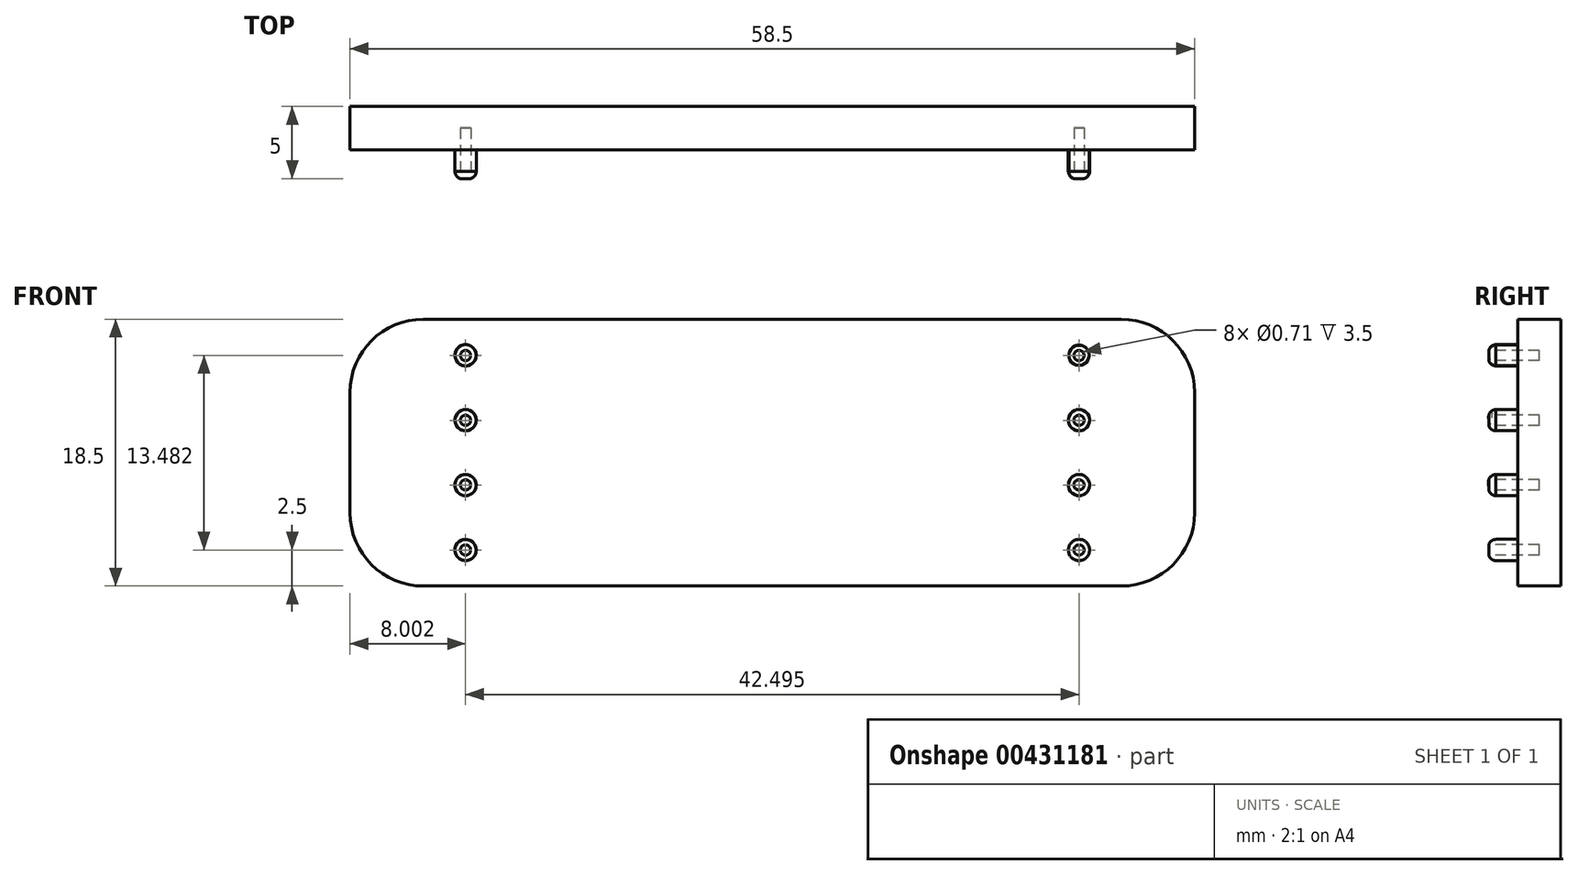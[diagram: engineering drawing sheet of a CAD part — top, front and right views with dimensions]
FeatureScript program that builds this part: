
annotation { "Feature Type Name" : "Feature", "Feature Type Description" : "" }
export const myFeature = defineFeature(function(context is Context, id is Id, definition is map)
    precondition{}
    {
        {
            var Q0;
            Q0=qCreatedBy(makeId("Front.planeOp"),FACE);
            var sketch = newSketch(context, id + "F0", { "sketchPlane" : qUnion([Q0])});
            skLineSegment(sketch, "E0.bottom", {"start": v(29.25, 9.25) * mm, "end": v(-29.25, 9.25) * mm});
            skLineSegment(sketch, "E0.top", {"start": v(29.25, -9.25) * mm, "end": v(-29.25, -9.25) * mm});
            skLineSegment(sketch, "E0.left", {"start": v(29.25, 9.25) * mm, "end": v(29.25, -9.25) * mm});
            skLineSegment(sketch, "E0.right", {"start": v(-29.25, 9.25) * mm, "end": v(-29.25, -9.25) * mm});
            skPoint(sketch, "E0.middle", {"position": v(0, 0) * mm});
            skSolve(sketch);
        }
        {
            var Q0;
            Q0=makeQuery(id+"F0.imprint","IMPRINT",FACE,{"disambiguationData":[TD([[makeQuery(id+"F0.imprint","IMPRINT",EDGE,{"derivedFrom":sQuery(id+"F0.wireOp",EDGE,"E0.bottom")}),1.0]])]});
            extrude(context, id + "F1", {"entities" : qUnion([Q0]), "depth" : 3 * mm});
        }
        {
            var Q0;
            Q0=makeQuery(id+"F1.opExtrude","CAP_FACE",FACE,{"disambiguationData":[OSD([sQuery(id+"F0.wireOp",EDGE,"E0.bottom"),sQuery(id+"F0.wireOp",EDGE,"E0.top"),sQuery(id+"F0.wireOp",EDGE,"E0.left"),sQuery(id+"F0.wireOp",EDGE,"E0.right")])],"isStart":false});
            var sketch = newSketch(context, id + "F2", { "sketchPlane" : qUnion([Q0])});
            skCircle(sketch, "E1", {"center": v(21.25, 6.75) * mm, "radius": 0.7 * mm});
            skCircle(sketch, "E2", {"center": v(21.25, 2.25) * mm, "radius": 0.74 * mm});
            skCircle(sketch, "E3", {"center": v(21.25, -2.25) * mm, "radius": 0.74 * mm});
            skCircle(sketch, "E4", {"center": v(21.25, -6.75) * mm, "radius": 0.74 * mm});
            skCircle(sketch, "E5", {"center": v(-21.25, 6.75) * mm, "radius": 0.74 * mm});
            skCircle(sketch, "E6", {"center": v(-21.25, 2.25) * mm, "radius": 0.74 * mm});
            skCircle(sketch, "E7", {"center": v(-21.25, -2.25) * mm, "radius": 0.74 * mm});
            skCircle(sketch, "E8", {"center": v(-21.25, -6.75) * mm, "radius": 0.74 * mm});
            skSolve(sketch);
        }
        {
            var Q0;
            Q0 = qSketchRegion(id + "F2", true);
            extrude(context, id + "F3", {"entities" : qUnion([Q0]), "operationType" : NewBodyOperationType.ADD, "depth" : 2 * mm});
        }
        {
            var Q0;
            Q0=makeQuery(id+"F3.opExtrude","CAP_FACE",FACE,{"disambiguationData":[OSD([sQuery(id+"F2.wireOp",EDGE,"E4")])],"isStart":false});
            var sketch = newSketch(context, id + "F4", { "sketchPlane" : qUnion([Q0])});
            skCircle(sketch, "E9", {"center": v(21.25, -6.75) * mm, "radius": 0.36 * mm});
            skCircle(sketch, "E10", {"center": v(21.25, -2.24) * mm, "radius": 0.36 * mm});
            skCircle(sketch, "E11", {"center": v(21.25, 2.24) * mm, "radius": 0.36 * mm});
            skCircle(sketch, "E12", {"center": v(21.25, 6.73) * mm, "radius": 0.36 * mm});
            skCircle(sketch, "E13", {"center": v(-21.25, -6.75) * mm, "radius": 0.36 * mm});
            skCircle(sketch, "E14", {"center": v(-21.25, -2.24) * mm, "radius": 0.36 * mm});
            skCircle(sketch, "E15", {"center": v(-21.25, 2.24) * mm, "radius": 0.36 * mm});
            skCircle(sketch, "E16", {"center": v(-21.25, 6.73) * mm, "radius": 0.36 * mm});
            skSolve(sketch);
        }
        {
            var Q0;
            Q0=makeQuery(id+"F4.imprint","IMPRINT",FACE,{"disambiguationData":[TD([[makeQuery(id+"F4.imprint","IMPRINT",EDGE,{"derivedFrom":sQuery(id+"F4.wireOp",EDGE,"E10")}),1.0]])]});
            var Q1;
            Q1=makeQuery(id+"F4.imprint","IMPRINT",FACE,{"disambiguationData":[TD([[makeQuery(id+"F4.imprint","IMPRINT",EDGE,{"derivedFrom":sQuery(id+"F4.wireOp",EDGE,"E11")}),1.0]])]});
            var Q2;
            Q2=makeQuery(id+"F4.imprint","IMPRINT",FACE,{"disambiguationData":[TD([[makeQuery(id+"F4.imprint","IMPRINT",EDGE,{"derivedFrom":sQuery(id+"F4.wireOp",EDGE,"E12")}),1.0]])]});
            var Q3;
            Q3=makeQuery(id+"F4.imprint","IMPRINT",FACE,{"disambiguationData":[TD([[makeQuery(id+"F4.imprint","IMPRINT",EDGE,{"derivedFrom":sQuery(id+"F4.wireOp",EDGE,"E13")}),1.0]])]});
            var Q4;
            Q4=makeQuery(id+"F4.imprint","IMPRINT",FACE,{"disambiguationData":[TD([[makeQuery(id+"F4.imprint","IMPRINT",EDGE,{"derivedFrom":sQuery(id+"F4.wireOp",EDGE,"E14")}),1.0]])]});
            var Q5;
            Q5=makeQuery(id+"F4.imprint","IMPRINT",FACE,{"disambiguationData":[TD([[makeQuery(id+"F4.imprint","IMPRINT",EDGE,{"derivedFrom":sQuery(id+"F4.wireOp",EDGE,"E15")}),1.0]])]});
            var Q6;
            Q6=makeQuery(id+"F4.imprint","IMPRINT",FACE,{"disambiguationData":[TD([[makeQuery(id+"F4.imprint","IMPRINT",EDGE,{"derivedFrom":sQuery(id+"F4.wireOp",EDGE,"E9")}),1.0]])]});
            var Q7;
            Q7=makeQuery(id+"F4.imprint","IMPRINT",FACE,{"disambiguationData":[TD([[makeQuery(id+"F4.imprint","IMPRINT",EDGE,{"derivedFrom":sQuery(id+"F4.wireOp",EDGE,"E16")}),1.0]])]});
            extrude(context, id + "F5", {"entities" : qUnion([Q0, Q1, Q2, Q3, Q4, Q5, Q6, Q7]), "operationType" : NewBodyOperationType.REMOVE, "oppositeDirection" : true, "depth" : 3.5 * mm});
        }
        {
            var Q0;
            Q0=makeQuery(id+"F1.opExtrude","SWEPT_FACE",FACE,{"disambiguationData":[OSD([sQuery(id+"F0.wireOp",EDGE,"E0.left")])]});
            cPlane(context, id + "F6", {"entities" : qUnion([Q0]), "cplaneType" : CPlaneType.OFFSET, "offset" : 9 * mm, "oppositeDirection" : true, "width" : 152.4 * mm, "height" : 152.4 * mm});
        }
        {
            var Q0;
            Q0=makeQuery(id+"F3.opExtrude","CAP_EDGE",EDGE,{"disambiguationData":[OSD([sQuery(id+"F2.wireOp",EDGE,"E1")])],"isStart":false});
            var Q1;
            Q1=makeQuery(id+"F3.opExtrude","CAP_EDGE",EDGE,{"disambiguationData":[OSD([sQuery(id+"F2.wireOp",EDGE,"E2")])],"isStart":false});
            var Q2;
            Q2=makeQuery(id+"F3.opExtrude","CAP_EDGE",EDGE,{"disambiguationData":[OSD([sQuery(id+"F2.wireOp",EDGE,"E3")])],"isStart":false});
            var Q3;
            Q3=makeQuery(id+"F3.opExtrude","CAP_EDGE",EDGE,{"disambiguationData":[OSD([sQuery(id+"F2.wireOp",EDGE,"E4")])],"isStart":false});
            var Q4;
            Q4=makeQuery(id+"F3.opExtrude","CAP_EDGE",EDGE,{"disambiguationData":[OSD([sQuery(id+"F2.wireOp",EDGE,"E5")])],"isStart":false});
            var Q5;
            Q5=makeQuery(id+"F3.opExtrude","CAP_EDGE",EDGE,{"disambiguationData":[OSD([sQuery(id+"F2.wireOp",EDGE,"E6")])],"isStart":false});
            var Q6;
            Q6=makeQuery(id+"F3.opExtrude","CAP_EDGE",EDGE,{"disambiguationData":[OSD([sQuery(id+"F2.wireOp",EDGE,"E7")])],"isStart":false});
            var Q7;
            Q7=makeQuery(id+"F3.opExtrude","CAP_EDGE",EDGE,{"disambiguationData":[OSD([sQuery(id+"F2.wireOp",EDGE,"E8")])],"isStart":false});
            fillet(context, id + "F7", {"entities" : qUnion([Q0, Q1, Q2, Q3, Q4, Q5, Q6, Q7]), "radius" : 0.5 * mm, "tangentPropagation" : true, "allowEdgeOverflow" : false});
        }
        {
            var Q0;
            Q0=makeQuery(id+"F1.opExtrude","SWEPT_EDGE",EDGE,{"disambiguationData":[OSD([sQuery(id+"F0.wireOp",EDGE,"E0.bottom"),sQuery(id+"F0.wireOp",EDGE,"E0.left")])]});
            fillet(context, id + "F8", {"entities" : qUnion([Q0]), "tangentPropagation" : true, "radius" : 5.08 * mm, "defaultsChanged" : false, "vertexSettings" : [], "allowEdgeOverflow" : false});
        }
        {
            var Q0;
            Q0=makeQuery(id+"F1.opExtrude","SWEPT_EDGE",EDGE,{"disambiguationData":[OSD([sQuery(id+"F0.wireOp",EDGE,"E0.top"),sQuery(id+"F0.wireOp",EDGE,"E0.left")])]});
            fillet(context, id + "F9", {"entities" : qUnion([Q0]), "tangentPropagation" : true, "radius" : 5.08 * mm, "defaultsChanged" : false, "vertexSettings" : [], "allowEdgeOverflow" : false});
        }
        {
            var Q0;
            Q0=makeQuery(id+"F1.opExtrude","SWEPT_EDGE",EDGE,{"disambiguationData":[OSD([sQuery(id+"F0.wireOp",EDGE,"E0.top"),sQuery(id+"F0.wireOp",EDGE,"E0.right")])]});
            fillet(context, id + "F10", {"entities" : qUnion([Q0]), "tangentPropagation" : true, "radius" : 5.08 * mm, "defaultsChanged" : false, "vertexSettings" : [], "allowEdgeOverflow" : false});
        }
        {
            var Q0;
            Q0=makeQuery(id+"F1.opExtrude","SWEPT_EDGE",EDGE,{"disambiguationData":[OSD([sQuery(id+"F0.wireOp",EDGE,"E0.bottom"),sQuery(id+"F0.wireOp",EDGE,"E0.right")])]});
            fillet(context, id + "F11", {"entities" : qUnion([Q0]), "tangentPropagation" : true, "radius" : 5.08 * mm, "defaultsChanged" : false, "vertexSettings" : [], "allowEdgeOverflow" : false});
        }
    });
